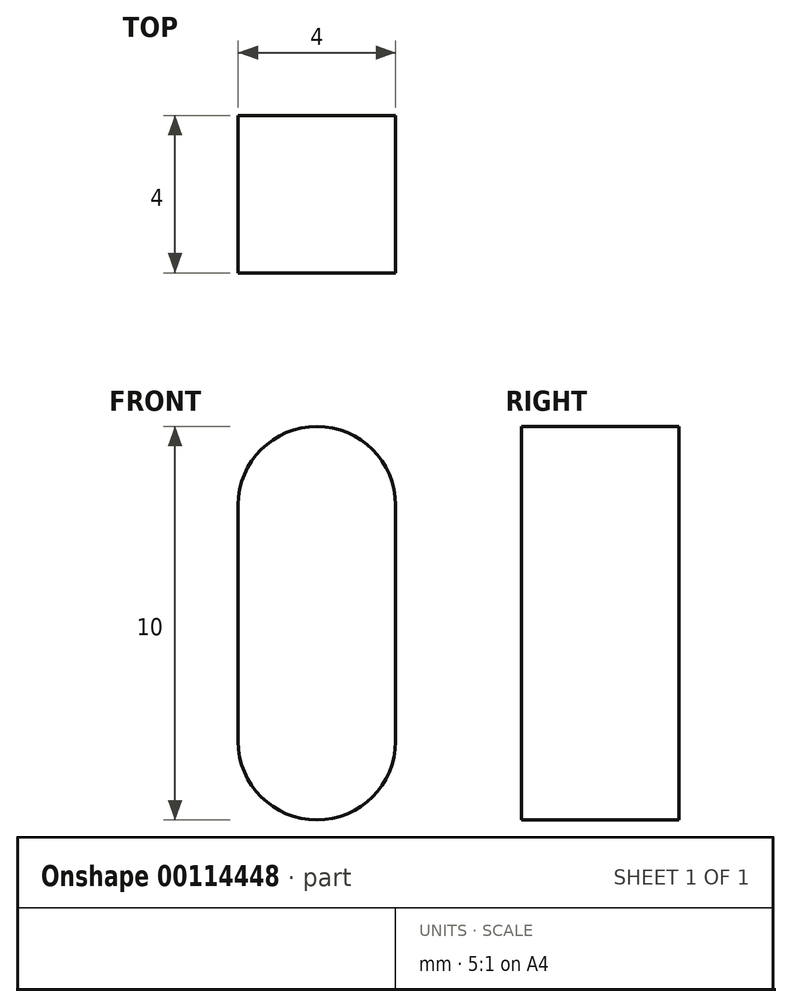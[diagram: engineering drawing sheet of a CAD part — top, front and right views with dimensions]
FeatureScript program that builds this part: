
annotation { "Feature Type Name" : "Feature", "Feature Type Description" : "" }
export const myFeature = defineFeature(function(context is Context, id is Id, definition is map)
    precondition{}
    {
        {
            var Q0;
            Q0=qCreatedBy(makeId("Front.planeOp"),FACE);
            var sketch = newSketch(context, id + "F0", { "sketchPlane" : qUnion([Q0])});
            skLineSegment(sketch, "E0.bottom", {"start": v(2, -5) * mm, "end": v(-2, -5) * mm});
            skLineSegment(sketch, "E0.top", {"start": v(2, 5) * mm, "end": v(-2, 5) * mm});
            skLineSegment(sketch, "E0.left", {"start": v(2, -5) * mm, "end": v(2, 5) * mm});
            skLineSegment(sketch, "E0.right", {"start": v(-2, -5) * mm, "end": v(-2, 5) * mm});
            skPoint(sketch, "E0.middle", {"position": v(0, 0) * mm});
            skSolve(sketch);
        }
        {
            var Q0;
            Q0 = qSketchRegion(id + "F0", true);
            extrude(context, id + "F1", {"entities" : qUnion([Q0]), "depth" : 4 * mm});
        }
        {
            var Q0;
            Q0=makeQuery(id+"F1.opExtrude","SWEPT_EDGE",EDGE,{"disambiguationData":[OSD([sQuery(id+"F0.wireOp",EDGE,"E0.top"),sQuery(id+"F0.wireOp",EDGE,"E0.left")])]});
            var Q1;
            Q1=makeQuery(id+"F1.opExtrude","SWEPT_EDGE",EDGE,{"disambiguationData":[OSD([sQuery(id+"F0.wireOp",EDGE,"E0.bottom"),sQuery(id+"F0.wireOp",EDGE,"E0.left")])]});
            var Q2;
            Q2=makeQuery(id+"F1.opExtrude","SWEPT_EDGE",EDGE,{"disambiguationData":[OSD([sQuery(id+"F0.wireOp",EDGE,"E0.top"),sQuery(id+"F0.wireOp",EDGE,"E0.right")])]});
            var Q3;
            Q3=makeQuery(id+"F1.opExtrude","SWEPT_EDGE",EDGE,{"disambiguationData":[OSD([sQuery(id+"F0.wireOp",EDGE,"E0.bottom"),sQuery(id+"F0.wireOp",EDGE,"E0.right")])]});
            fillet(context, id + "F2", {"entities" : qUnion([Q0, Q1, Q2, Q3]), "radius" : 2 * mm, "tangentPropagation" : true, "allowEdgeOverflow" : false});
        }
    });
